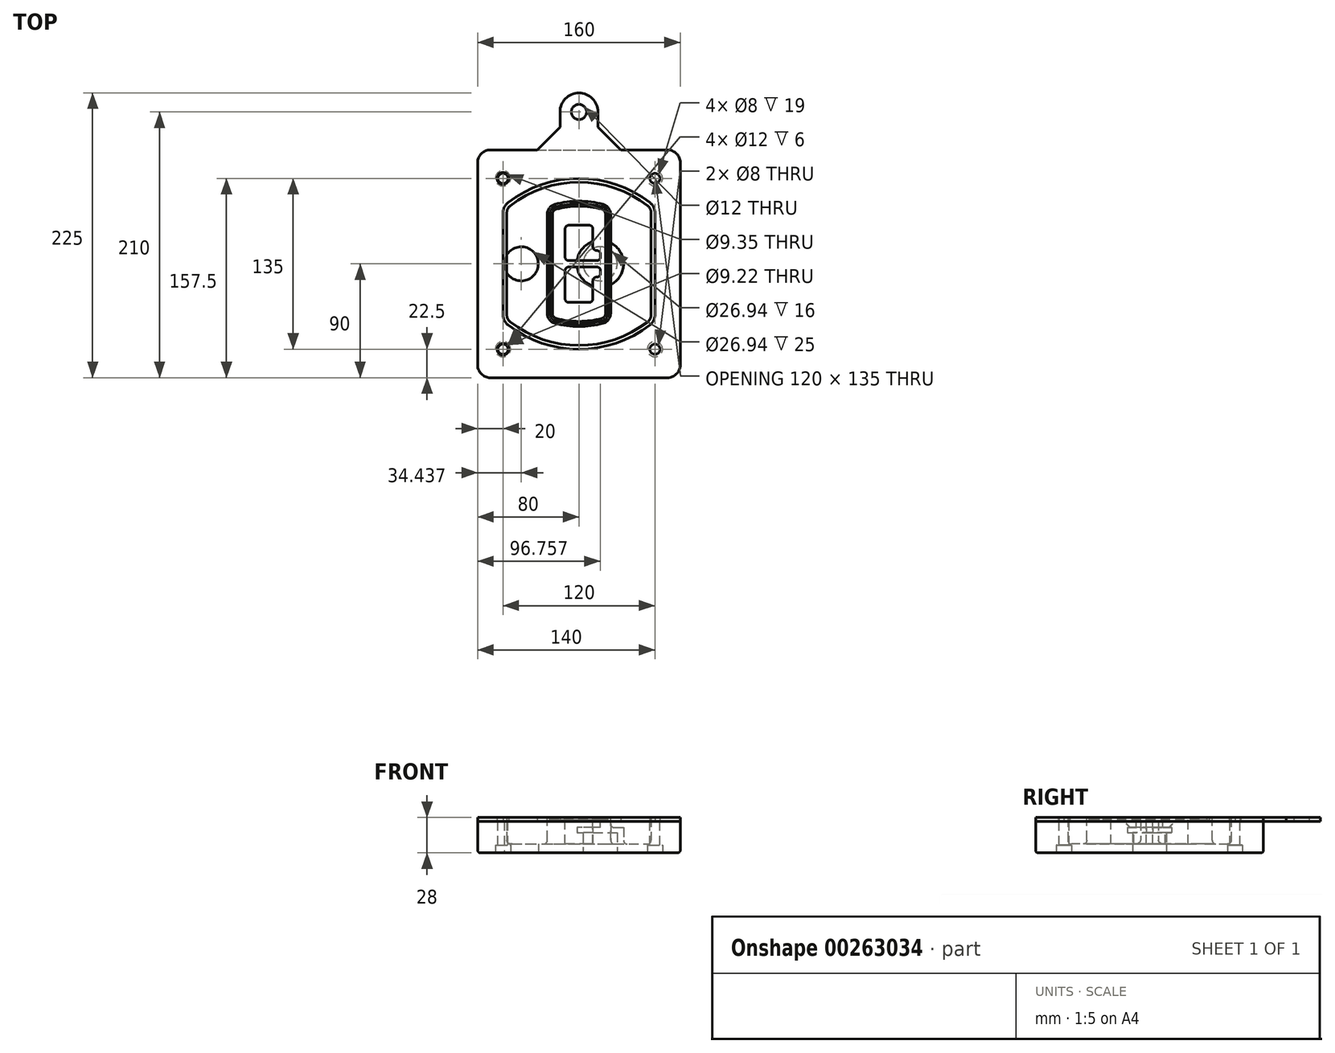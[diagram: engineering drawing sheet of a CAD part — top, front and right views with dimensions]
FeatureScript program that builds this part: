
annotation { "Feature Type Name" : "Feature", "Feature Type Description" : "" }
export const myFeature = defineFeature(function(context is Context, id is Id, definition is map)
    precondition{}
    {
        {
            var Q0;
            Q0=qCreatedBy(makeId("Top.planeOp"),FACE);
            var sketch = newSketch(context, id + "F0", { "sketchPlane" : qUnion([Q0])});
            skPoint(sketch, "E0.rect.middle", {"position": v(0, 0) * mm});
            skLineSegment(sketch, "E1.bottom", {"start": v(-70, -90) * mm, "end": v(70, -90) * mm});
            skLineSegment(sketch, "E1.top", {"start": v(-70, 90) * mm, "end": v(70, 90) * mm});
            skLineSegment(sketch, "E1.left", {"start": v(-80, -80) * mm, "end": v(-80, 80) * mm});
            skLineSegment(sketch, "E1.right", {"start": v(80, -80) * mm, "end": v(80, 80) * mm});
            skLineSegment(sketch, "E2", {"start": v(-80, 90) * mm, "end": v(80, -90) * mm, "construction": true});
            skLineSegment(sketch, "E3", {"start": v(80, 90) * mm, "end": v(-80, -90) * mm, "construction": true});
            skCircle(sketch, "E4", {"center": v(-60, 67.5) * mm, "radius": 4 * mm});
            skCircle(sketch, "E5", {"center": v(60, 67.5) * mm, "radius": 4 * mm});
            skCircle(sketch, "E6", {"center": v(60, -67.5) * mm, "radius": 4 * mm});
            skCircle(sketch, "E7", {"center": v(-60, -67.5) * mm, "radius": 4 * mm});
            skLineSegment(sketch, "E8", {"start": v(-60, 67.5) * mm, "end": v(60, 67.5) * mm, "construction": true});
            skLineSegment(sketch, "E9", {"start": v(60, 67.5) * mm, "end": v(60, -67.5) * mm, "construction": true});
            skLineSegment(sketch, "E10", {"start": v(60, -67.5) * mm, "end": v(-60, -67.5) * mm, "construction": true});
            skLineSegment(sketch, "E11", {"start": v(-60, -67.5) * mm, "end": v(-60, 67.5) * mm, "construction": true});
            skLineSegment(sketch, "E12", {"start": v(-60, 40.3) * mm, "end": v(-60, -40.3) * mm});
            skLineSegment(sketch, "E13", {"start": v(60, 40.3) * mm, "end": v(60, -40.3) * mm});
            skArc(sketch, "E14", {"start": v(56.15, 48.18) * mm, "mid": v(0, 67.5) * mm, "end": v(-56.15, 48.18) * mm});
            skArc(sketch, "E15", {"start": v(-56.15, -48.18) * mm, "mid": v(0, -67.5) * mm, "end": v(56.15, -48.18) * mm});
            skLineSegment(sketch, "E16", {"start": v(-60, 0) * mm, "end": v(60, 0) * mm, "construction": true});
            skPoint(sketch, "E17.visualSharp", {"position": v(-60, -45) * mm});
            skArc(sketch, "E17.filletArc", {"start": v(-60, -40.3) * mm, "mid": v(-58.99, -44.68) * mm, "end": v(-56.15, -48.18) * mm});
            skPoint(sketch, "E18.visualSharp", {"position": v(-60, 45) * mm});
            skArc(sketch, "E18.filletArc", {"start": v(-56.15, 48.18) * mm, "mid": v(-58.99, 44.68) * mm, "end": v(-60, 40.3) * mm});
            skPoint(sketch, "E19.visualSharp", {"position": v(60, 45) * mm});
            skArc(sketch, "E19.filletArc", {"start": v(60, 40.3) * mm, "mid": v(58.99, 44.68) * mm, "end": v(56.15, 48.18) * mm});
            skPoint(sketch, "E20.visualSharp", {"position": v(60, -45) * mm});
            skArc(sketch, "E20.filletArc", {"start": v(56.15, -48.18) * mm, "mid": v(58.99, -44.68) * mm, "end": v(60, -40.3) * mm});
            skPoint(sketch, "E21.visualSharp", {"position": v(-80, 90) * mm});
            skArc(sketch, "E21.filletArc", {"start": v(-70, 90) * mm, "mid": v(-77.07, 87.07) * mm, "end": v(-80, 80) * mm});
            skPoint(sketch, "E22.visualSharp", {"position": v(80, 90) * mm});
            skArc(sketch, "E22.filletArc", {"start": v(80, 80) * mm, "mid": v(77.07, 87.07) * mm, "end": v(70, 90) * mm});
            skPoint(sketch, "E23.visualSharp", {"position": v(80, -90) * mm});
            skArc(sketch, "E23.filletArc", {"start": v(70, -90) * mm, "mid": v(77.07, -87.07) * mm, "end": v(80, -80) * mm});
            skPoint(sketch, "E24.visualSharp", {"position": v(-80, -90) * mm});
            skArc(sketch, "E24.filletArc", {"start": v(-80, -80) * mm, "mid": v(-77.07, -87.07) * mm, "end": v(-70, -90) * mm});
            skArc(sketch, "E25.0", {"start": v(57, 40.3) * mm, "mid": v(56.3, 43.36) * mm, "end": v(54.3, 45.81) * mm});
            skLineSegment(sketch, "E25.1", {"start": v(57, 40.3) * mm, "end": v(57, -40.3) * mm});
            skArc(sketch, "E25.2", {"start": v(54.3, -45.81) * mm, "mid": v(56.3, -43.36) * mm, "end": v(57, -40.3) * mm});
            skArc(sketch, "E25.3", {"start": v(-54.3, -45.81) * mm, "mid": v(0, -64.5) * mm, "end": v(54.3, -45.81) * mm});
            skArc(sketch, "E25.4", {"start": v(-57, -40.3) * mm, "mid": v(-56.3, -43.36) * mm, "end": v(-54.3, -45.81) * mm});
            skArc(sketch, "E25.5", {"start": v(54.3, 45.81) * mm, "mid": v(0, 64.5) * mm, "end": v(-54.3, 45.81) * mm});
            skLineSegment(sketch, "E25.6", {"start": v(-57, 40.3) * mm, "end": v(-57, -40.3) * mm});
            skArc(sketch, "E25.7", {"start": v(-54.3, 45.81) * mm, "mid": v(-56.3, 43.36) * mm, "end": v(-57, 40.3) * mm});
            skArc(sketch, "E26.0", {"start": v(-58.62, 51.33) * mm, "mid": v(-62.58, 46.43) * mm, "end": v(-64, 40.3) * mm});
            skArc(sketch, "E26.1", {"start": v(58.62, 51.33) * mm, "mid": v(0, 71.5) * mm, "end": v(-58.62, 51.33) * mm});
            skArc(sketch, "E26.2", {"start": v(64, 40.3) * mm, "mid": v(62.58, 46.43) * mm, "end": v(58.62, 51.33) * mm});
            skLineSegment(sketch, "E26.3", {"start": v(64, 40.3) * mm, "end": v(64, -40.3) * mm});
            skArc(sketch, "E26.4", {"start": v(58.62, -51.33) * mm, "mid": v(62.58, -46.43) * mm, "end": v(64, -40.3) * mm});
            skLineSegment(sketch, "E26.5", {"start": v(-64, 40.3) * mm, "end": v(-64, -40.3) * mm});
            skArc(sketch, "E26.6", {"start": v(-58.62, -51.33) * mm, "mid": v(0, -71.5) * mm, "end": v(58.62, -51.33) * mm});
            skArc(sketch, "E26.7", {"start": v(-64, -40.3) * mm, "mid": v(-62.58, -46.43) * mm, "end": v(-58.62, -51.33) * mm});
            skSolve(sketch);
        }
        {
            var Q0;
            Q0=makeQuery(id+"F0.imprint","IMPRINT",FACE,{"disambiguationData":[TD([[makeQuery(id+"F0.imprint","IMPRINT",EDGE,{"derivedFrom":sQuery(id+"F0.wireOp",EDGE,"E1.bottom")}),1.0]])]});
            var Q1;
            Q1=makeQuery(id+"F0.imprint","IMPRINT",FACE,{"disambiguationData":[TD([[makeQuery(id+"F0.imprint","IMPRINT",EDGE,{"derivedFrom":sQuery(id+"F0.wireOp",EDGE,"E12")}),1.0]])]});
            var Q2;
            Q2=makeQuery(id+"F0.imprint","IMPRINT",FACE,{"disambiguationData":[TD([[makeQuery(id+"F0.imprint","IMPRINT",EDGE,{"derivedFrom":sQuery(id+"F0.wireOp",EDGE,"E25.0")}),1.0]])]});
            var Q3;
            Q3=makeQuery(id+"F0.imprint","IMPRINT",FACE,{"disambiguationData":[TD([[makeQuery(id+"F0.imprint","IMPRINT",EDGE,{"derivedFrom":sQuery(id+"F0.wireOp",EDGE,"E12")}),-1.0]])]});
            extrude(context, id + "F1", {"entities" : qUnion([Q0, Q1, Q2, Q3]), "oppositeDirection" : true, "depth" : 25 * mm});
        }
        {
            var Q0;
            Q0=makeQuery(id+"F0.imprint","IMPRINT",FACE,{"disambiguationData":[TD([[makeQuery(id+"F0.imprint","IMPRINT",EDGE,{"derivedFrom":sQuery(id+"F0.wireOp",EDGE,"E12")}),1.0]])]});
            extrude(context, id + "F2", {"entities" : qUnion([Q0]), "operationType" : NewBodyOperationType.ADD, "depth" : 3 * mm});
        }
        {
            var Q0;
            Q0=makeQuery(id+"F0.imprint","IMPRINT",FACE,{"disambiguationData":[TD([[makeQuery(id+"F0.imprint","IMPRINT",EDGE,{"derivedFrom":sQuery(id+"F0.wireOp",EDGE,"E25.0")}),1.0]])]});
            extrude(context, id + "F3", {"entities" : qUnion([Q0]), "operationType" : NewBodyOperationType.REMOVE, "oppositeDirection" : true, "depth" : 18 * mm});
        }
        {
            var Q0;
            Q0=makeQuery(id+"F2.opExtrude","CAP_FACE",FACE,{"disambiguationData":[OSD([sQuery(id+"F0.wireOp",EDGE,"E12"),sQuery(id+"F0.wireOp",EDGE,"E13"),sQuery(id+"F0.wireOp",EDGE,"E14"),sQuery(id+"F0.wireOp",EDGE,"E15"),sQuery(id+"F0.wireOp",EDGE,"E17.filletArc"),sQuery(id+"F0.wireOp",EDGE,"E18.filletArc"),sQuery(id+"F0.wireOp",EDGE,"E19.filletArc"),sQuery(id+"F0.wireOp",EDGE,"E20.filletArc"),sQuery(id+"F0.wireOp",EDGE,"E25.0"),sQuery(id+"F0.wireOp",EDGE,"E25.1"),sQuery(id+"F0.wireOp",EDGE,"E25.2"),sQuery(id+"F0.wireOp",EDGE,"E25.3"),sQuery(id+"F0.wireOp",EDGE,"E25.4"),sQuery(id+"F0.wireOp",EDGE,"E25.5"),sQuery(id+"F0.wireOp",EDGE,"E25.6"),sQuery(id+"F0.wireOp",EDGE,"E25.7")])],"isStart":false});
            var sketch = newSketch(context, id + "F4", { "sketchPlane" : qUnion([Q0])});
            skArc(sketch, "E27.0", {"start": v(-19.08, -46.97) * mm, "mid": v(0, -49.5) * mm, "end": v(19.08, -46.97) * mm});
            skArc(sketch, "E28.0", {"start": v(19.08, 46.97) * mm, "mid": v(0, 49.5) * mm, "end": v(-19.08, 46.97) * mm});
            skLineSegment(sketch, "E29", {"start": v(-25, 39.25) * mm, "end": v(-25, -39.25) * mm});
            skLineSegment(sketch, "E30", {"start": v(25, 39.25) * mm, "end": v(25, -39.25) * mm});
            skLineSegment(sketch, "E31", {"start": v(-25, 45.1) * mm, "end": v(25, 45.1) * mm, "construction": true});
            skLineSegment(sketch, "E32", {"start": v(-25, -45.1) * mm, "end": v(25, -45.1) * mm, "construction": true});
            skPoint(sketch, "E33.visualSharp", {"position": v(-25, 45.1) * mm});
            skArc(sketch, "E33.filletArc", {"start": v(-19.08, 46.97) * mm, "mid": v(-23.35, 44.11) * mm, "end": v(-25, 39.25) * mm});
            skPoint(sketch, "E34.visualSharp", {"position": v(25, 45.1) * mm});
            skArc(sketch, "E34.filletArc", {"start": v(25, 39.25) * mm, "mid": v(23.35, 44.11) * mm, "end": v(19.08, 46.97) * mm});
            skPoint(sketch, "E35.visualSharp", {"position": v(25, -45.1) * mm});
            skArc(sketch, "E35.filletArc", {"start": v(19.08, -46.97) * mm, "mid": v(23.35, -44.11) * mm, "end": v(25, -39.25) * mm});
            skPoint(sketch, "E36.visualSharp", {"position": v(-25, -45.1) * mm});
            skArc(sketch, "E36.filletArc", {"start": v(-25, -39.25) * mm, "mid": v(-23.35, -44.11) * mm, "end": v(-19.08, -46.97) * mm});
            skArc(sketch, "E37.0", {"start": v(54.3, 45.81) * mm, "mid": v(0, 64.5) * mm, "end": v(-54.3, 45.81) * mm});
            skArc(sketch, "E37.1", {"start": v(-54.3, 45.81) * mm, "mid": v(-56.3, 43.36) * mm, "end": v(-57, 40.3) * mm});
            skLineSegment(sketch, "E37.2", {"start": v(-57, 40.3) * mm, "end": v(-57, -40.3) * mm});
            skArc(sketch, "E37.3", {"start": v(-57, -40.3) * mm, "mid": v(-56.3, -43.36) * mm, "end": v(-54.3, -45.81) * mm});
            skArc(sketch, "E37.4", {"start": v(-54.3, -45.81) * mm, "mid": v(0, -64.5) * mm, "end": v(54.3, -45.81) * mm});
            skArc(sketch, "E37.5", {"start": v(54.3, -45.81) * mm, "mid": v(56.3, -43.36) * mm, "end": v(57, -40.3) * mm});
            skLineSegment(sketch, "E37.6", {"start": v(57, 40.3) * mm, "end": v(57, -40.3) * mm});
            skArc(sketch, "E37.7", {"start": v(57, 40.3) * mm, "mid": v(56.3, 43.36) * mm, "end": v(54.3, 45.81) * mm});
            skLineSegment(sketch, "E38.0", {"start": v(23, 39.25) * mm, "end": v(23, -39.25) * mm});
            skArc(sketch, "E38.1", {"start": v(18.56, -45.04) * mm, "mid": v(21.76, -42.9) * mm, "end": v(23, -39.25) * mm});
            skArc(sketch, "E38.2", {"start": v(-18.56, -45.04) * mm, "mid": v(0, -47.5) * mm, "end": v(18.56, -45.04) * mm});
            skArc(sketch, "E38.3", {"start": v(-23, -39.25) * mm, "mid": v(-21.76, -42.9) * mm, "end": v(-18.56, -45.04) * mm});
            skLineSegment(sketch, "E38.4", {"start": v(-23, 39.25) * mm, "end": v(-23, -39.25) * mm});
            skArc(sketch, "E38.5", {"start": v(23, 39.25) * mm, "mid": v(21.76, 42.9) * mm, "end": v(18.56, 45.04) * mm});
            skArc(sketch, "E38.6", {"start": v(-18.56, 45.04) * mm, "mid": v(-21.76, 42.9) * mm, "end": v(-23, 39.25) * mm});
            skArc(sketch, "E38.7", {"start": v(18.56, 45.04) * mm, "mid": v(0, 47.5) * mm, "end": v(-18.56, 45.04) * mm});
            skArc(sketch, "E39.0", {"start": v(21, 39.25) * mm, "mid": v(20.18, 41.68) * mm, "end": v(18.04, 43.1) * mm});
            skLineSegment(sketch, "E39.1", {"start": v(21, 39.25) * mm, "end": v(21, -39.25) * mm});
            skArc(sketch, "E39.2", {"start": v(18.04, -43.1) * mm, "mid": v(20.18, -41.68) * mm, "end": v(21, -39.25) * mm});
            skArc(sketch, "E39.3", {"start": v(-18.04, -43.1) * mm, "mid": v(0, -45.5) * mm, "end": v(18.04, -43.1) * mm});
            skArc(sketch, "E39.4", {"start": v(-21, -39.25) * mm, "mid": v(-20.18, -41.68) * mm, "end": v(-18.04, -43.1) * mm});
            skArc(sketch, "E39.5", {"start": v(18.04, 43.1) * mm, "mid": v(0, 45.5) * mm, "end": v(-18.04, 43.1) * mm});
            skLineSegment(sketch, "E39.6", {"start": v(-21, 39.25) * mm, "end": v(-21, -39.25) * mm});
            skArc(sketch, "E39.7", {"start": v(-18.04, 43.1) * mm, "mid": v(-20.18, 41.68) * mm, "end": v(-21, 39.25) * mm});
            skLineSegment(sketch, "E40", {"start": v(-25, 0) * mm, "end": v(25, 0) * mm, "construction": true});
            skLineSegment(sketch, "E41", {"start": v(-11, 5.5) * mm, "end": v(-11, 27.5) * mm});
            skLineSegment(sketch, "E42", {"start": v(-8, 30.5) * mm, "end": v(8, 30.5) * mm});
            skLineSegment(sketch, "E43", {"start": v(11, 27.5) * mm, "end": v(11, 13.5) * mm});
            skLineSegment(sketch, "E44", {"start": v(14, 10.5) * mm, "end": v(14, 10.5) * mm});
            skLineSegment(sketch, "E45", {"start": v(17, 7.5) * mm, "end": v(17, 5.5) * mm});
            skLineSegment(sketch, "E46", {"start": v(14, 2.5) * mm, "end": v(-8, 2.5) * mm});
            skPoint(sketch, "E47.visualSharp", {"position": v(-11, 30.5) * mm});
            skArc(sketch, "E47.filletArc", {"start": v(-8, 30.5) * mm, "mid": v(-10.12, 29.62) * mm, "end": v(-11, 27.5) * mm});
            skPoint(sketch, "E48.visualSharp", {"position": v(11, 30.5) * mm});
            skArc(sketch, "E48.filletArc", {"start": v(11, 27.5) * mm, "mid": v(10.12, 29.62) * mm, "end": v(8, 30.5) * mm});
            skPoint(sketch, "E49.visualSharp", {"position": v(11, 10.5) * mm});
            skArc(sketch, "E49.filletArc", {"start": v(11, 13.5) * mm, "mid": v(11.88, 11.38) * mm, "end": v(14, 10.5) * mm});
            skPoint(sketch, "E50.visualSharp", {"position": v(17, 10.5) * mm});
            skArc(sketch, "E50.filletArc", {"start": v(17, 7.5) * mm, "mid": v(16.12, 9.62) * mm, "end": v(14, 10.5) * mm});
            skPoint(sketch, "E51.visualSharp", {"position": v(17, 2.5) * mm});
            skArc(sketch, "E51.filletArc", {"start": v(14, 2.5) * mm, "mid": v(16.12, 3.38) * mm, "end": v(17, 5.5) * mm});
            skPoint(sketch, "E52.visualSharp", {"position": v(-11, 2.5) * mm});
            skArc(sketch, "E52.filletArc", {"start": v(-11, 5.5) * mm, "mid": v(-10.12, 3.38) * mm, "end": v(-8, 2.5) * mm});
            skLineSegment(sketch, "E53.0.MirrorCS", {"start": v(14, -2.5) * mm, "end": v(-8, -2.5) * mm});
            skArc(sketch, "E54.0.MirrorCS", {"start": v(-11, -5.5) * mm, "mid": v(-10.12, -3.38) * mm, "end": v(-8, -2.5) * mm});
            skLineSegment(sketch, "E55.0.MirrorCS", {"start": v(-11, -5.5) * mm, "end": v(-11, -27.5) * mm});
            skArc(sketch, "E56.0.MirrorCS", {"start": v(-8, -30.5) * mm, "mid": v(-10.12, -29.62) * mm, "end": v(-11, -27.5) * mm});
            skLineSegment(sketch, "E57.0.MirrorCS", {"start": v(-8, -30.5) * mm, "end": v(8, -30.5) * mm});
            skArc(sketch, "E58.0.MirrorCS", {"start": v(11, -27.5) * mm, "mid": v(10.12, -29.62) * mm, "end": v(8, -30.5) * mm});
            skLineSegment(sketch, "E59.0.MirrorCS", {"start": v(11, -27.5) * mm, "end": v(11, -13.5) * mm});
            skArc(sketch, "E60.0.MirrorCS", {"start": v(11, -13.5) * mm, "mid": v(11.88, -11.38) * mm, "end": v(14, -10.5) * mm});
            skArc(sketch, "E61.0.MirrorCS", {"start": v(17, -7.5) * mm, "mid": v(16.12, -9.62) * mm, "end": v(14, -10.5) * mm});
            skLineSegment(sketch, "E62.0.MirrorCS", {"start": v(17, -7.5) * mm, "end": v(17, -5.5) * mm});
            skArc(sketch, "E63.0.MirrorCS", {"start": v(14, -2.5) * mm, "mid": v(16.12, -3.38) * mm, "end": v(17, -5.5) * mm});
            skSolve(sketch);
        }
        {
            var Q0;
            Q0=makeQuery(id+"F4.imprint","IMPRINT",FACE,{"disambiguationData":[TD([[makeQuery(id+"F4.imprint","IMPRINT",EDGE,{"derivedFrom":sQuery(id+"F4.wireOp",EDGE,"E27.0")}),1.0]])]});
            var Q1;
            Q1=makeQuery(id+"F4.imprint","IMPRINT",FACE,{"disambiguationData":[TD([[makeQuery(id+"F4.imprint","IMPRINT",EDGE,{"derivedFrom":sQuery(id+"F4.wireOp",EDGE,"E38.0")}),-1.0]])]});
            var Q2;
            Q2=makeQuery(id+"F4.imprint","IMPRINT",FACE,{"disambiguationData":[TD([[makeQuery(id+"F4.imprint","IMPRINT",EDGE,{"derivedFrom":sQuery(id+"F4.wireOp",EDGE,"E39.0")}),1.0]])]});
            extrude(context, id + "F5", {"entities" : qUnion([Q0, Q1, Q2]), "operationType" : NewBodyOperationType.ADD, "endBound" : BoundingType.UP_TO_NEXT, "oppositeDirection" : true, "depth" : 25 * mm});
        }
        {
            var Q0;
            Q0=makeQuery(id+"F4.imprint","IMPRINT",FACE,{"disambiguationData":[TD([[makeQuery(id+"F4.imprint","IMPRINT",EDGE,{"derivedFrom":sQuery(id+"F4.wireOp",EDGE,"E38.0")}),-1.0]])]});
            extrude(context, id + "F6", {"entities" : qUnion([Q0]), "operationType" : NewBodyOperationType.REMOVE, "oppositeDirection" : true, "depth" : 2 * mm});
        }
        {
            var Q0;
            Q0=makeQuery(id+"F1.opExtrude","CAP_FACE",FACE,{"disambiguationData":[OSD([sQuery(id+"F0.wireOp",EDGE,"E1.bottom"),sQuery(id+"F0.wireOp",EDGE,"E1.top"),sQuery(id+"F0.wireOp",EDGE,"E1.left"),sQuery(id+"F0.wireOp",EDGE,"E1.right"),sQuery(id+"F0.wireOp",EDGE,"E4"),sQuery(id+"F0.wireOp",EDGE,"E5"),sQuery(id+"F0.wireOp",EDGE,"E6"),sQuery(id+"F0.wireOp",EDGE,"E7"),sQuery(id+"F0.wireOp",EDGE,"E21.filletArc"),sQuery(id+"F0.wireOp",EDGE,"E22.filletArc"),sQuery(id+"F0.wireOp",EDGE,"E23.filletArc"),sQuery(id+"F0.wireOp",EDGE,"E24.filletArc")])],"isStart":false});
            var sketch = newSketch(context, id + "F7", { "sketchPlane" : qUnion([Q0])});
            skCircle(sketch, "E64", {"center": v(16.76, 0) * mm, "radius": 13.47 * mm});
            skCircle(sketch, "E65", {"center": v(-45.56, 0) * mm, "radius": 13.47 * mm});
            skLineSegment(sketch, "E66", {"start": v(80, 0) * mm, "end": v(-80, 0) * mm});
            skCircle(sketch, "E67", {"center": v(16.76, 0) * mm, "radius": 18.47 * mm});
            skCircle(sketch, "E68", {"center": v(60, -67.5) * mm, "radius": 6 * mm});
            skCircle(sketch, "E69", {"center": v(-60, -67.5) * mm, "radius": 6 * mm});
            skCircle(sketch, "E70", {"center": v(-60, 67.5) * mm, "radius": 6 * mm});
            skCircle(sketch, "E71", {"center": v(60, 67.5) * mm, "radius": 6 * mm});
            skSolve(sketch);
        }
        {
            var Q0;
            {var subQ1=sQuery(id+"F7.wireOp",EDGE,"E66");var subQ4=sQuery(id+"F7.wireOp",EDGE,"E64");var subQ6=makeQuery(id+"F7.imprint","INTERSECT",VERTEX,{"disambiguationData":[OD(0.0)],"derivedFrom":[subQ4,subQ1]});Q0=makeQuery(id+"F7.imprint","IMPRINT",FACE,{"disambiguationData":[TD([[makeQuery(id+"F7.imprint","IMPRINT",EDGE,{"disambiguationData":[TD([[subQ6,-1.0]])],"derivedFrom":subQ4}),-1.0]])]});}
            var Q1;
            {var subQ0=sQuery(id+"F7.wireOp",EDGE,"E66");var subQ1=sQuery(id+"F7.wireOp",EDGE,"E64");var subQ3=makeQuery(id+"F7.imprint","INTERSECT",VERTEX,{"disambiguationData":[OD(0.0)],"derivedFrom":[subQ1,subQ0]});Q1=makeQuery(id+"F7.imprint","IMPRINT",FACE,{"disambiguationData":[TD([[makeQuery(id+"F7.imprint","IMPRINT",EDGE,{"disambiguationData":[TD([[subQ3,-1.0]])],"derivedFrom":subQ1}),1.0]])]});}
            var Q2;
            {var subQ0=sQuery(id+"F7.wireOp",EDGE,"E66");var subQ1=sQuery(id+"F7.wireOp",EDGE,"E64");var subQ3=makeQuery(id+"F7.imprint","INTERSECT",VERTEX,{"disambiguationData":[OD(0.0)],"derivedFrom":[subQ1,subQ0]});Q2=makeQuery(id+"F7.imprint","IMPRINT",FACE,{"disambiguationData":[TD([[makeQuery(id+"F7.imprint","IMPRINT",EDGE,{"disambiguationData":[TD([[subQ3,1.0]])],"derivedFrom":subQ1}),1.0]])]});}
            var Q3;
            {var subQ1=sQuery(id+"F7.wireOp",EDGE,"E66");var subQ4=sQuery(id+"F7.wireOp",EDGE,"E64");var subQ6=makeQuery(id+"F7.imprint","INTERSECT",VERTEX,{"disambiguationData":[OD(0.0)],"derivedFrom":[subQ4,subQ1]});Q3=makeQuery(id+"F7.imprint","IMPRINT",FACE,{"disambiguationData":[TD([[makeQuery(id+"F7.imprint","IMPRINT",EDGE,{"disambiguationData":[TD([[subQ6,1.0]])],"derivedFrom":subQ4}),-1.0]])]});}
            extrude(context, id + "F8", {"entities" : qUnion([Q0, Q1, Q2, Q3]), "operationType" : NewBodyOperationType.ADD, "oppositeDirection" : true, "depth" : 20 * mm});
        }
        {
            var Q0;
            {var subQ0=sQuery(id+"F7.wireOp",EDGE,"E66");var subQ1=sQuery(id+"F7.wireOp",EDGE,"E64");var subQ3=makeQuery(id+"F7.imprint","INTERSECT",VERTEX,{"disambiguationData":[OD(0.0)],"derivedFrom":[subQ1,subQ0]});Q0=makeQuery(id+"F7.imprint","IMPRINT",FACE,{"disambiguationData":[TD([[makeQuery(id+"F7.imprint","IMPRINT",EDGE,{"disambiguationData":[TD([[subQ3,-1.0]])],"derivedFrom":subQ1}),1.0]])]});}
            var Q1;
            {var subQ0=sQuery(id+"F7.wireOp",EDGE,"E66");var subQ1=sQuery(id+"F7.wireOp",EDGE,"E64");var subQ3=makeQuery(id+"F7.imprint","INTERSECT",VERTEX,{"disambiguationData":[OD(0.0)],"derivedFrom":[subQ1,subQ0]});Q1=makeQuery(id+"F7.imprint","IMPRINT",FACE,{"disambiguationData":[TD([[makeQuery(id+"F7.imprint","IMPRINT",EDGE,{"disambiguationData":[TD([[subQ3,1.0]])],"derivedFrom":subQ1}),1.0]])]});}
            extrude(context, id + "F9", {"entities" : qUnion([Q0, Q1]), "operationType" : NewBodyOperationType.REMOVE, "oppositeDirection" : true, "depth" : 16 * mm});
        }
        {
            var Q0;
            {var subQ0=sQuery(id+"F7.wireOp",EDGE,"E66");var subQ1=sQuery(id+"F7.wireOp",EDGE,"E65");var subQ3=makeQuery(id+"F7.imprint","INTERSECT",VERTEX,{"disambiguationData":[OD(0.0)],"derivedFrom":[subQ1,subQ0]});Q0=makeQuery(id+"F7.imprint","IMPRINT",FACE,{"disambiguationData":[TD([[makeQuery(id+"F7.imprint","IMPRINT",EDGE,{"disambiguationData":[TD([[subQ3,-1.0]])],"derivedFrom":subQ1}),1.0]])]});}
            var Q1;
            {var subQ0=sQuery(id+"F7.wireOp",EDGE,"E66");var subQ1=sQuery(id+"F7.wireOp",EDGE,"E65");var subQ3=makeQuery(id+"F7.imprint","INTERSECT",VERTEX,{"disambiguationData":[OD(0.0)],"derivedFrom":[subQ1,subQ0]});Q1=makeQuery(id+"F7.imprint","IMPRINT",FACE,{"disambiguationData":[TD([[makeQuery(id+"F7.imprint","IMPRINT",EDGE,{"disambiguationData":[TD([[subQ3,1.0]])],"derivedFrom":subQ1}),1.0]])]});}
            extrude(context, id + "F10", {"entities" : qUnion([Q0, Q1]), "operationType" : NewBodyOperationType.REMOVE, "oppositeDirection" : true, "depth" : 25 * mm});
        }
        {
            var Q0;
            Q0=makeQuery(id+"F7.imprint","IMPRINT",FACE,{"disambiguationData":[TD([[makeQuery(id+"F7.imprint","IMPRINT",EDGE,{"derivedFrom":sQuery(id+"F7.wireOp",EDGE,"E68")}),1.0]])]});
            var Q1;
            Q1=makeQuery(id+"F7.imprint","IMPRINT",FACE,{"disambiguationData":[TD([[makeQuery(id+"F7.imprint","IMPRINT",EDGE,{"derivedFrom":makeQuery(id+"F1.opExtrude","CAP_EDGE",EDGE,{"disambiguationData":[OSD([sQuery(id+"F0.wireOp",EDGE,"E5")])],"isStart":false})}),-1.0]])]});
            var Q2;
            Q2=makeQuery(id+"F7.imprint","IMPRINT",FACE,{"disambiguationData":[TD([[makeQuery(id+"F7.imprint","IMPRINT",EDGE,{"derivedFrom":sQuery(id+"F7.wireOp",EDGE,"E69")}),1.0]])]});
            var Q3;
            Q3=makeQuery(id+"F7.imprint","IMPRINT",FACE,{"disambiguationData":[TD([[makeQuery(id+"F7.imprint","IMPRINT",EDGE,{"derivedFrom":makeQuery(id+"F1.opExtrude","CAP_EDGE",EDGE,{"disambiguationData":[OSD([sQuery(id+"F0.wireOp",EDGE,"E4")])],"isStart":false})}),-1.0]])]});
            var Q4;
            Q4=makeQuery(id+"F7.imprint","IMPRINT",FACE,{"disambiguationData":[TD([[makeQuery(id+"F7.imprint","IMPRINT",EDGE,{"derivedFrom":sQuery(id+"F7.wireOp",EDGE,"E70")}),1.0]])]});
            var Q5;
            Q5=makeQuery(id+"F7.imprint","IMPRINT",FACE,{"disambiguationData":[TD([[makeQuery(id+"F7.imprint","IMPRINT",EDGE,{"derivedFrom":makeQuery(id+"F1.opExtrude","CAP_EDGE",EDGE,{"disambiguationData":[OSD([sQuery(id+"F0.wireOp",EDGE,"E7")])],"isStart":false})}),-1.0]])]});
            var Q6;
            Q6=makeQuery(id+"F7.imprint","IMPRINT",FACE,{"disambiguationData":[TD([[makeQuery(id+"F7.imprint","IMPRINT",EDGE,{"derivedFrom":sQuery(id+"F7.wireOp",EDGE,"E71")}),1.0]])]});
            var Q7;
            Q7=makeQuery(id+"F7.imprint","IMPRINT",FACE,{"disambiguationData":[TD([[makeQuery(id+"F7.imprint","IMPRINT",EDGE,{"derivedFrom":makeQuery(id+"F1.opExtrude","CAP_EDGE",EDGE,{"disambiguationData":[OSD([sQuery(id+"F0.wireOp",EDGE,"E6")])],"isStart":false})}),-1.0]])]});
            extrude(context, id + "F11", {"entities" : qUnion([Q0, Q1, Q2, Q3, Q4, Q5, Q6, Q7]), "operationType" : NewBodyOperationType.REMOVE, "oppositeDirection" : true, "depth" : 6 * mm});
        }
        {
            var Q0;
            Q0=makeQuery(id+"F9.boolean.opBoolean","COPY",FACE,{"derivedFrom":makeQuery(id+"F9.opExtrude","CAP_FACE",FACE,{"disambiguationData":[OSD([sQuery(id+"F7.wireOp",EDGE,"E64")])],"isStart":false})});
            var sketch = newSketch(context, id + "F12", { "sketchPlane" : qUnion([Q0])});
            skArc(sketch, "E72.0", {"start": v(11, 17.55) * mm, "mid": v(2.57, 11.82) * mm, "end": v(-1.54, 2.5) * mm});
            skArc(sketch, "E72.1", {"start": v(-1.54, -2.5) * mm, "mid": v(2.57, -11.82) * mm, "end": v(11, -17.55) * mm});
            skLineSegment(sketch, "E73", {"start": v(-1.54, -2.5) * mm, "end": v(14, -2.5) * mm});
            skLineSegment(sketch, "E74.0", {"start": v(14, 2.5) * mm, "end": v(-1.54, 2.5) * mm});
            skArc(sketch, "E74.1", {"start": v(14, 2.5) * mm, "mid": v(16.12, 3.38) * mm, "end": v(17, 5.5) * mm});
            skLineSegment(sketch, "E74.2", {"start": v(17, 7.5) * mm, "end": v(17, 5.5) * mm});
            skArc(sketch, "E74.3", {"start": v(17, 7.5) * mm, "mid": v(16.12, 9.62) * mm, "end": v(14, 10.5) * mm});
            skArc(sketch, "E74.4", {"start": v(11, 13.5) * mm, "mid": v(11.88, 11.38) * mm, "end": v(14, 10.5) * mm});
            skLineSegment(sketch, "E74.5", {"start": v(11, 17.55) * mm, "end": v(11, 13.5) * mm});
            skLineSegment(sketch, "E74.7", {"start": v(14, -2.5) * mm, "end": v(-1.54, -2.5) * mm});
            skArc(sketch, "E74.8", {"start": v(14, -2.5) * mm, "mid": v(16.12, -3.38) * mm, "end": v(17, -5.5) * mm});
            skLineSegment(sketch, "E74.9", {"start": v(17, -7.5) * mm, "end": v(17, -5.5) * mm});
            skArc(sketch, "E74.10", {"start": v(17, -7.5) * mm, "mid": v(16.12, -9.62) * mm, "end": v(14, -10.5) * mm});
            skArc(sketch, "E74.11", {"start": v(11, -13.5) * mm, "mid": v(11.88, -11.38) * mm, "end": v(14, -10.5) * mm});
            skLineSegment(sketch, "E74.12", {"start": v(11, -17.55) * mm, "end": v(11, -13.5) * mm});
            skPoint(sketch, "E75.orphan", {"position": v(11, -27.5) * mm});
            skPoint(sketch, "E76.orphan", {"position": v(-8, -2.5) * mm});
            skPoint(sketch, "E77.orphan", {"position": v(-8, 2.5) * mm});
            skPoint(sketch, "E78.orphan", {"position": v(11, 27.5) * mm});
            skSolve(sketch);
        }
        {
            var Q0;
            {var subQ7=sQuery(id+"F12.wireOp",EDGE,"E72.0");var subQ14=sQuery(id+"F12.wireOp",EDGE,"E72.1");var subQ16=sQuery(id+"F12.wireOp",EDGE,"E74.1");var subQ18=sQuery(id+"F12.wireOp",EDGE,"E74.8");Q0=qUnion([makeQuery(id+"F12.imprint","IMPRINT",FACE,{"disambiguationData":[TD([[makeQuery(id+"F12.imprint","IMPRINT",EDGE,{"derivedFrom":subQ7}),1.0]])]}),makeQuery(id+"F12.imprint","IMPRINT",FACE,{"disambiguationData":[TD([[makeQuery(id+"F12.imprint","IMPRINT",EDGE,{"derivedFrom":subQ14}),1.0]])]}),makeQuery(id+"F12.imprint","IMPRINT",FACE,{"disambiguationData":[TD([[makeQuery(id+"F12.imprint","IMPRINT",EDGE,{"derivedFrom":subQ16}),1.0]])]}),makeQuery(id+"F12.imprint","IMPRINT",FACE,{"disambiguationData":[TD([[makeQuery(id+"F12.imprint","IMPRINT",EDGE,{"derivedFrom":subQ18}),-1.0]])]})]);}
            var Q1;
            Q1=makeQuery(id+"F5.boolean.opBoolean","SPLIT",FACE,{"disambiguationData":[TD([makeQuery(id+"F5.opExtrude","SWEPT_FACE",FACE,{"disambiguationData":[OSD([sQuery(id+"F4.wireOp",EDGE,"E41")])]})])],"derivedFrom":makeQuery(id+"F3.boolean.opBoolean","COPY",FACE,{"derivedFrom":makeQuery(id+"F3.opExtrude","CAP_FACE",FACE,{"disambiguationData":[OSD([sQuery(id+"F0.wireOp",EDGE,"E25.0"),sQuery(id+"F0.wireOp",EDGE,"E25.1"),sQuery(id+"F0.wireOp",EDGE,"E25.2"),sQuery(id+"F0.wireOp",EDGE,"E25.3"),sQuery(id+"F0.wireOp",EDGE,"E25.4"),sQuery(id+"F0.wireOp",EDGE,"E25.5"),sQuery(id+"F0.wireOp",EDGE,"E25.6"),sQuery(id+"F0.wireOp",EDGE,"E25.7")])],"isStart":false})})});
            extrude(context, id + "F13", {"entities" : qUnion([Q0]), "operationType" : NewBodyOperationType.REMOVE, "endBound" : BoundingType.UP_TO_SURFACE, "endBoundEntityFace" : qUnion([Q1]), "depth" : 25 * mm});
        }
        {
            var Q0;
            Q0=makeQuery(id+"F3.boolean.opBoolean","COPY",EDGE,{"derivedFrom":makeQuery(id+"F3.opExtrude","CAP_EDGE",EDGE,{"disambiguationData":[OSD([sQuery(id+"F0.wireOp",EDGE,"E25.6")])],"isStart":false})});
            var Q1;
            Q1=makeQuery(id+"F8.boolean.opBoolean","INTERSECT",EDGE,{"derivedFrom":[makeQuery(id+"F5.opExtrude","SWEPT_FACE",FACE,{"disambiguationData":[OSD([sQuery(id+"F4.wireOp",EDGE,"E30")])]}),makeQuery(id+"F8.opExtrude","CAP_FACE",FACE,{"disambiguationData":[OSD([sQuery(id+"F7.wireOp",EDGE,"E67")])],"isStart":false})]});
            var Q2;
            Q2=makeQuery(id+"F8.boolean.opBoolean","INTERSECT",EDGE,{"disambiguationData":[OD(1.0)],"derivedFrom":[makeQuery(id+"F5.opExtrude","SWEPT_FACE",FACE,{"disambiguationData":[OSD([sQuery(id+"F4.wireOp",EDGE,"E30")])]}),makeQuery(id+"F8.opExtrude","SWEPT_FACE",FACE,{"disambiguationData":[OSD([sQuery(id+"F7.wireOp",EDGE,"E67")])]})]});
            var Q3;
            {var subQ0=sQuery(id+"F4.wireOp",EDGE,"E30");Q3=makeQuery(id+"F8.boolean.opBoolean","SPLIT",EDGE,{"disambiguationData":[TD([makeQuery(id+"F5.opExtrude","SWEPT_FACE",FACE,{"disambiguationData":[OSD([sQuery(id+"F4.wireOp",EDGE,"E35.filletArc")])]})])],"derivedFrom":makeQuery(id+"F5.opExtrude","CAP_EDGE",EDGE,{"disambiguationData":[OSD([subQ0])],"isStart":false})});}
            var Q4;
            {var subQ0=sQuery(id+"F0.wireOp",EDGE,"E25.7");var subQ1=sQuery(id+"F0.wireOp",EDGE,"E25.1");var subQ2=sQuery(id+"F0.wireOp",EDGE,"E25.6");var subQ3=sQuery(id+"F0.wireOp",EDGE,"E25.5");var subQ4=sQuery(id+"F0.wireOp",EDGE,"E25.4");var subQ5=sQuery(id+"F0.wireOp",EDGE,"E25.0");var subQ6=sQuery(id+"F0.wireOp",EDGE,"E25.2");var subQ7=sQuery(id+"F0.wireOp",EDGE,"E25.3");Q4=makeQuery(id+"F8.boolean.opBoolean","INTERSECT",EDGE,{"derivedFrom":[makeQuery(id+"F5.boolean.opBoolean","SPLIT",FACE,{"disambiguationData":[TD([makeQuery(id+"F2.opExtrude","SWEPT_FACE",FACE,{"disambiguationData":[OSD([subQ5])]})])],"derivedFrom":makeQuery(id+"F3.boolean.opBoolean","COPY",FACE,{"derivedFrom":makeQuery(id+"F3.opExtrude","CAP_FACE",FACE,{"disambiguationData":[OSD([subQ5,subQ1,subQ6,subQ7,subQ4,subQ3,subQ2,subQ0])],"isStart":false})})}),makeQuery(id+"F8.opExtrude","SWEPT_FACE",FACE,{"disambiguationData":[OSD([sQuery(id+"F7.wireOp",EDGE,"E67")])]})]});}
            var Q5;
            Q5=makeQuery(id+"F8.boolean.opBoolean","INTERSECT",EDGE,{"disambiguationData":[OD(0.0)],"derivedFrom":[makeQuery(id+"F5.opExtrude","SWEPT_FACE",FACE,{"disambiguationData":[OSD([sQuery(id+"F4.wireOp",EDGE,"E30")])]}),makeQuery(id+"F8.opExtrude","SWEPT_FACE",FACE,{"disambiguationData":[OSD([sQuery(id+"F7.wireOp",EDGE,"E67")])]})]});
            fillet(context, id + "F14", {"entities" : qUnion([Q0, Q1, Q2, Q3, Q4, Q5]), "radius" : 3 * mm, "tangentPropagation" : true, "allowEdgeOverflow" : false});
        }
        {
            var Q0;
            Q0=makeQuery(id+"F1.opExtrude","CAP_EDGE",EDGE,{"disambiguationData":[OSD([sQuery(id+"F0.wireOp",EDGE,"E1.bottom")])],"isStart":false});
            fillet(context, id + "F15", {"entities" : qUnion([Q0]), "radius" : 2 * mm, "tangentPropagation" : true, "allowEdgeOverflow" : false});
        }
        {
            var Q0;
            {var subQ0=sQuery(id+"F0.wireOp",EDGE,"E22.filletArc");var subQ1=sQuery(id+"F0.wireOp",EDGE,"E7");var subQ2=sQuery(id+"F0.wireOp",EDGE,"E6");var subQ3=sQuery(id+"F0.wireOp",EDGE,"E5");var subQ4=sQuery(id+"F0.wireOp",EDGE,"E4");var subQ5=sQuery(id+"F0.wireOp",EDGE,"E1.bottom");var subQ6=sQuery(id+"F0.wireOp",EDGE,"E21.filletArc");var subQ7=sQuery(id+"F0.wireOp",EDGE,"E1.top");var subQ8=sQuery(id+"F0.wireOp",EDGE,"E1.left");var subQ9=sQuery(id+"F0.wireOp",EDGE,"E1.right");var subQ10=sQuery(id+"F0.wireOp",EDGE,"E23.filletArc");var subQ11=sQuery(id+"F0.wireOp",EDGE,"E24.filletArc");Q0=makeQuery(id+"F2.boolean.opBoolean","SPLIT",FACE,{"disambiguationData":[TD([makeQuery(id+"F1.opExtrude","SWEPT_FACE",FACE,{"disambiguationData":[OSD([subQ5])]})])],"derivedFrom":makeQuery(id+"F1.opExtrude","CAP_FACE",FACE,{"disambiguationData":[OSD([subQ5,subQ7,subQ8,subQ9,subQ4,subQ3,subQ2,subQ1,subQ6,subQ0,subQ10,subQ11])],"isStart":true})});}
            var sketch = newSketch(context, id + "F16", { "sketchPlane" : qUnion([Q0])});
            skLineSegment(sketch, "E79", {"start": v(-33, 90) * mm, "end": v(33, 90) * mm});
            skLineSegment(sketch, "E80", {"start": v(-33, 90) * mm, "end": v(-15, 108) * mm});
            skLineSegment(sketch, "E81", {"start": v(33, 90) * mm, "end": v(15, 108) * mm});
            skLineSegment(sketch, "E82", {"start": v(-15, 108) * mm, "end": v(-15, 120) * mm});
            skLineSegment(sketch, "E83", {"start": v(15, 108) * mm, "end": v(15, 120) * mm});
            skArc(sketch, "E84", {"start": v(15, 120) * mm, "mid": v(0, 135) * mm, "end": v(-15, 120) * mm});
            skCircle(sketch, "E85", {"center": v(0, 120) * mm, "radius": 6 * mm});
            skLineSegment(sketch, "E86", {"start": v(-80, 0) * mm, "end": v(80, 0) * mm, "construction": true});
            skLineSegment(sketch, "E87", {"start": v(-266.38, 127.05) * mm, "end": v(-273.35, 127.05) * mm});
            skLineSegment(sketch, "E88.MirrorCS", {"start": v(-33, -90) * mm, "end": v(33, -90) * mm});
            skLineSegment(sketch, "E89.MirrorCS", {"start": v(-33, -90) * mm, "end": v(-15, -108) * mm});
            skLineSegment(sketch, "E90.MirrorCS", {"start": v(-15, -108) * mm, "end": v(-15, -120) * mm});
            skArc(sketch, "E91.MirrorCS", {"start": v(15, -120) * mm, "mid": v(0, -135) * mm, "end": v(-15, -120) * mm});
            skLineSegment(sketch, "E92.MirrorCS", {"start": v(33, -90) * mm, "end": v(15, -108) * mm});
            skLineSegment(sketch, "E93.MirrorCS", {"start": v(15, -108) * mm, "end": v(15, -120) * mm});
            skCircle(sketch, "E94", {"center": v(0, -120) * mm, "radius": 6 * mm});
            skLineSegment(sketch, "E95", {"start": v(-70, -90) * mm, "end": v(70, -90) * mm});
            skLineSegment(sketch, "E96", {"start": v(-80, -80) * mm, "end": v(-80, 80) * mm});
            skLineSegment(sketch, "E97", {"start": v(80, -80) * mm, "end": v(80, 80) * mm});
            skLineSegment(sketch, "E98", {"start": v(-70, 90) * mm, "end": v(70, 90) * mm});
            skArc(sketch, "E99", {"start": v(-70, 90) * mm, "mid": v(-77.07, 87.07) * mm, "end": v(-80, 80) * mm});
            skArc(sketch, "E100", {"start": v(-80, -80) * mm, "mid": v(-77.07, -87.07) * mm, "end": v(-70, -90) * mm});
            skArc(sketch, "E101", {"start": v(70, -90) * mm, "mid": v(77.07, -87.07) * mm, "end": v(80, -80) * mm});
            skArc(sketch, "E102", {"start": v(80, 80) * mm, "mid": v(77.07, 87.07) * mm, "end": v(70, 90) * mm});
            skCircle(sketch, "E103", {"center": v(60, 67.5) * mm, "radius": 3.18 * mm});
            skCircle(sketch, "E104", {"center": v(60, -67.5) * mm, "radius": 3.18 * mm});
            skCircle(sketch, "E105", {"center": v(-60, 67.5) * mm, "radius": 4.68 * mm});
            skCircle(sketch, "E106", {"center": v(-60, -67.5) * mm, "radius": 4.61 * mm});
            skSolve(sketch);
        }
        {
            var Q0;
            Q0=makeQuery(id+"F16.imprint","IMPRINT",FACE,{"disambiguationData":[TD([[makeQuery(id+"F16.imprint","IMPRINT",EDGE,{"derivedFrom":sQuery(id+"F16.wireOp",EDGE,"E96")}),-1.0]])]});
            var Q1;
            {var subQ1=sQuery(id+"F16.wireOp",EDGE,"E80");Q1=makeQuery(id+"F16.imprint","IMPRINT",FACE,{"disambiguationData":[TD([[makeQuery(id+"F16.imprint","IMPRINT",EDGE,{"derivedFrom":subQ1}),-1.0]])]});}
            var Q2;
            Q2=makeQuery(id+"F16.imprint","IMPRINT",FACE,{"disambiguationData":[TD([[makeQuery(id+"F16.imprint","IMPRINT",EDGE,{"derivedFrom":sQuery(id+"F16.wireOp",EDGE,"E91.MirrorCS")}),-1.0]])]});
            var Q3;
            Q3=makeQuery(id+"F2.opExtrude","CAP_FACE",FACE,{"disambiguationData":[OSD([sQuery(id+"F0.wireOp",EDGE,"E12"),sQuery(id+"F0.wireOp",EDGE,"E13"),sQuery(id+"F0.wireOp",EDGE,"E14"),sQuery(id+"F0.wireOp",EDGE,"E15"),sQuery(id+"F0.wireOp",EDGE,"E17.filletArc"),sQuery(id+"F0.wireOp",EDGE,"E18.filletArc"),sQuery(id+"F0.wireOp",EDGE,"E19.filletArc"),sQuery(id+"F0.wireOp",EDGE,"E20.filletArc"),sQuery(id+"F0.wireOp",EDGE,"E25.0"),sQuery(id+"F0.wireOp",EDGE,"E25.1"),sQuery(id+"F0.wireOp",EDGE,"E25.2"),sQuery(id+"F0.wireOp",EDGE,"E25.3"),sQuery(id+"F0.wireOp",EDGE,"E25.4"),sQuery(id+"F0.wireOp",EDGE,"E25.5"),sQuery(id+"F0.wireOp",EDGE,"E25.6"),sQuery(id+"F0.wireOp",EDGE,"E25.7")])],"isStart":false});
            extrude(context, id + "F17", {"entities" : qUnion([Q0, Q1, Q2]), "endBound" : BoundingType.UP_TO_SURFACE, "endBoundEntityFace" : qUnion([Q3]), "depth" : 10 * mm});
        }
    });
